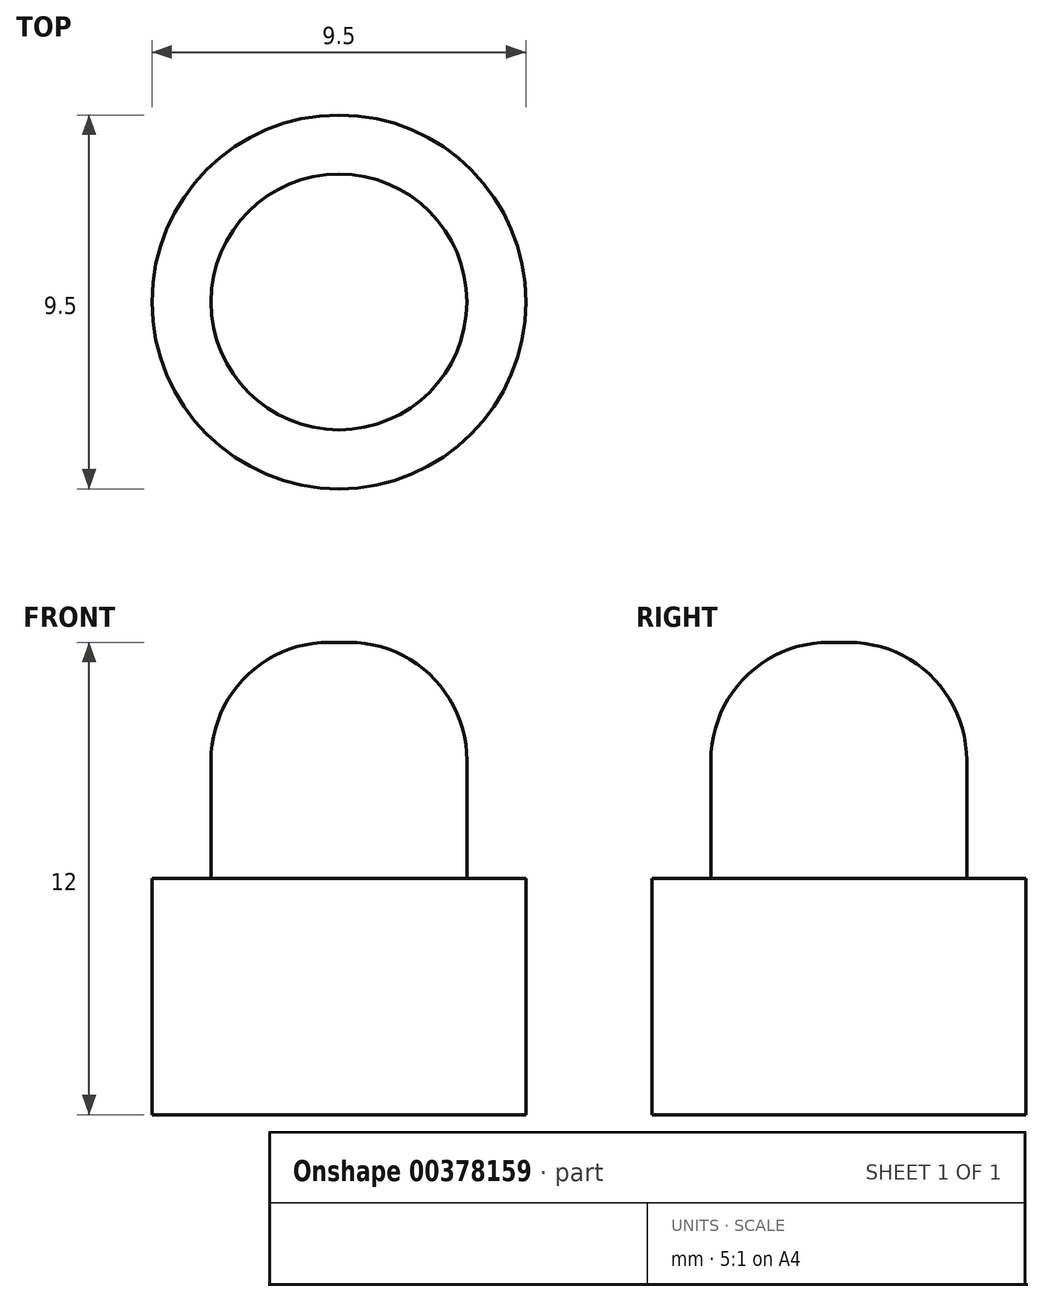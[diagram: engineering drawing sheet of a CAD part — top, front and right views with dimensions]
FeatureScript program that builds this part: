
annotation { "Feature Type Name" : "Feature", "Feature Type Description" : "" }
export const myFeature = defineFeature(function(context is Context, id is Id, definition is map)
    precondition{}
    {
        {
            var Q0;
            Q0=qCreatedBy(makeId("Top.planeOp"),FACE);
            var sketch = newSketch(context, id + "F0", { "sketchPlane" : qUnion([Q0])});
            skCircle(sketch, "E0", {"center": v(0, 0) * mm, "radius": 4.75 * mm});
            skCircle(sketch, "E1", {"center": v(0, 0) * mm, "radius": 3.25 * mm});
            skSolve(sketch);
        }
        {
            var Q0;
            Q0=makeQuery(id+"F0.imprint","IMPRINT",FACE,{"disambiguationData":[TD([[makeQuery(id+"F0.imprint","IMPRINT",EDGE,{"derivedFrom":sQuery(id+"F0.wireOp",EDGE,"E1")}),1.0]])]});
            extrude(context, id + "F1", {"entities" : qUnion([Q0]), "depth" : 12 * mm});
        }
        {
            var Q0;
            Q0=makeQuery(id+"F0.imprint","IMPRINT",FACE,{"disambiguationData":[TD([[makeQuery(id+"F0.imprint","IMPRINT",EDGE,{"derivedFrom":sQuery(id+"F0.wireOp",EDGE,"E0")}),1.0]])]});
            var Q1;
            Q1=sQuery(id+"F0.wireOp",EDGE,"E0");
            extrude(context, id + "F2", {"entities" : qUnion([Q0]), "operationType" : NewBodyOperationType.ADD, "surfaceEntities" : qUnion([Q1]), "depth" : 6 * mm});
        }
        {
            var Q0;
            Q0=makeQuery(id+"F1.opExtrude","CAP_FACE",FACE,{"disambiguationData":[OSD([sQuery(id+"F0.wireOp",EDGE,"E1")])],"isStart":false});
            fillet(context, id + "F3", {"entities" : qUnion([Q0]), "radius" : 3 * mm, "tangentPropagation" : true, "allowEdgeOverflow" : false});
        }
    });
